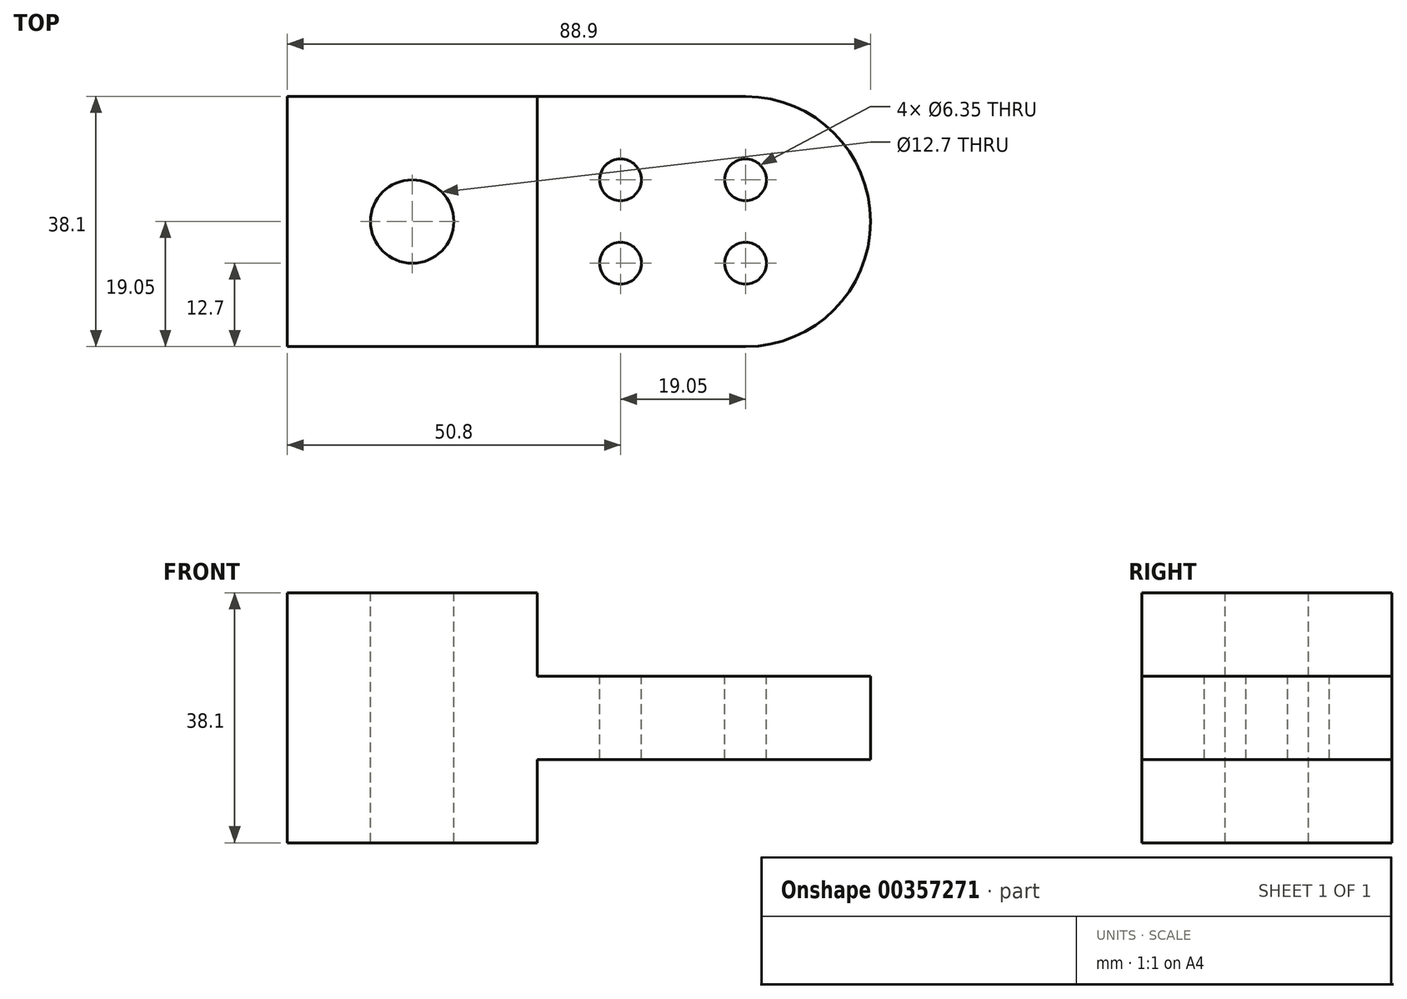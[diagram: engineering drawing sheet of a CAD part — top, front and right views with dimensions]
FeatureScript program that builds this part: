
annotation { "Feature Type Name" : "Feature", "Feature Type Description" : "" }
export const myFeature = defineFeature(function(context is Context, id is Id, definition is map)
    precondition{}
    {
        {
            var Q0;
            Q0=qCreatedBy(makeId("Front.planeOp"),FACE);
            var sketch = newSketch(context, id + "F0", { "sketchPlane" : qUnion([Q0])});
            skLineSegment(sketch, "E0", {"start": v(0, 6.35) * mm, "end": v(0, 19.05) * mm});
            skLineSegment(sketch, "E1", {"start": v(0, 19.05) * mm, "end": v(-38.1, 19.05) * mm});
            skLineSegment(sketch, "E2", {"start": v(-38.1, 19.05) * mm, "end": v(-38.1, -19.05) * mm});
            skLineSegment(sketch, "E3", {"start": v(-38.1, -19.05) * mm, "end": v(0, -19.05) * mm});
            skLineSegment(sketch, "E4", {"start": v(0, -19.05) * mm, "end": v(0, -6.35) * mm});
            skLineSegment(sketch, "E5", {"start": v(0, -6.35) * mm, "end": v(50.8, -6.35) * mm});
            skLineSegment(sketch, "E6", {"start": v(50.8, -6.35) * mm, "end": v(50.8, 6.35) * mm});
            skLineSegment(sketch, "E7", {"start": v(50.8, 6.35) * mm, "end": v(0, 6.35) * mm});
            skPoint(sketch, "E8", {"position": v(-38.1, 0) * mm});
            skSolve(sketch);
        }
        {
            var Q0;
            Q0=makeQuery(id+"F0.imprint","IMPRINT",FACE,{"disambiguationData":[TD([[makeQuery(id+"F0.imprint","IMPRINT",EDGE,{"derivedFrom":sQuery(id+"F0.wireOp",EDGE,"E0")}),1.0]])]});
            extrude(context, id + "F1", {"entities" : qUnion([Q0]), "endBound" : BoundingType.SYMMETRIC, "depth" : 38.1 * mm});
        }
        {
            var Q0;
            Q0=makeQuery(id+"F1.opExtrude","SWEPT_FACE",FACE,{"disambiguationData":[OSD([sQuery(id+"F0.wireOp",EDGE,"E7")])]});
            var sketch = newSketch(context, id + "F2", { "sketchPlane" : qUnion([Q0])});
            skArc(sketch, "E9", {"start": v(31.75, -19.05) * mm, "mid": v(50.8, 0) * mm, "end": v(31.75, 19.05) * mm});
            skLineSegment(sketch, "E10", {"start": v(31.75, 19.05) * mm, "end": v(50.8, 19.05) * mm});
            skLineSegment(sketch, "E11", {"start": v(50.8, 19.05) * mm, "end": v(50.8, 0) * mm});
            skLineSegment(sketch, "E12", {"start": v(31.75, -19.05) * mm, "end": v(50.8, -19.05) * mm});
            skLineSegment(sketch, "E13", {"start": v(50.8, -19.05) * mm, "end": v(50.8, 0) * mm});
            skSolve(sketch);
        }
        {
            var Q0;
            Q0 = qSketchRegion(id + "F2", true);
            extrude(context, id + "F3", {"entities" : qUnion([Q0]), "operationType" : NewBodyOperationType.REMOVE, "oppositeDirection" : true, "depth" : 25.4 * mm});
        }
        {
            var Q0;
            Q0 = qSketchRegion(id + "F2", true);
            extrude(context, id + "F4", {"entities" : qUnion([Q0]), "operationType" : NewBodyOperationType.REMOVE, "oppositeDirection" : true, "depth" : 25.4 * mm});
        }
        {
            var Q0;
            {var subQ0=sQuery(id+"F0.wireOp",EDGE,"E7");var subQ2=makeQuery(id+"F1.opExtrude","SWEPT_EDGE",EDGE,{"disambiguationData":[OSD([sQuery(id+"F0.wireOp",EDGE,"E0"),subQ0])]});Q0=makeQuery(id+"F2.imprint","IMPRINT",FACE,{"disambiguationData":[TD([[makeQuery(id+"F2.imprint","IMPRINT",EDGE,{"derivedFrom":subQ2}),-1.0]])]});}
            var sketch = newSketch(context, id + "F5", { "sketchPlane" : qUnion([Q0])});
            skCircle(sketch, "E14", {"center": v(12.7, 6.35) * mm, "radius": 3.18 * mm});
            skCircle(sketch, "E15", {"center": v(31.75, 6.35) * mm, "radius": 3.18 * mm});
            skCircle(sketch, "E16", {"center": v(12.7, -6.35) * mm, "radius": 3.18 * mm});
            skCircle(sketch, "E17", {"center": v(31.75, -6.35) * mm, "radius": 3.18 * mm});
            skCircle(sketch, "E18", {"center": v(-19.05, 0) * mm, "radius": 6.35 * mm});
            skSolve(sketch);
        }
        {
            var Q0;
            Q0 = qSketchRegion(id + "F5", true);
            extrude(context, id + "F6", {"entities" : qUnion([Q0]), "operationType" : NewBodyOperationType.REMOVE, "endBound" : BoundingType.SYMMETRIC, "oppositeDirection" : true, "depth" : 127 * mm});
        }
    });
